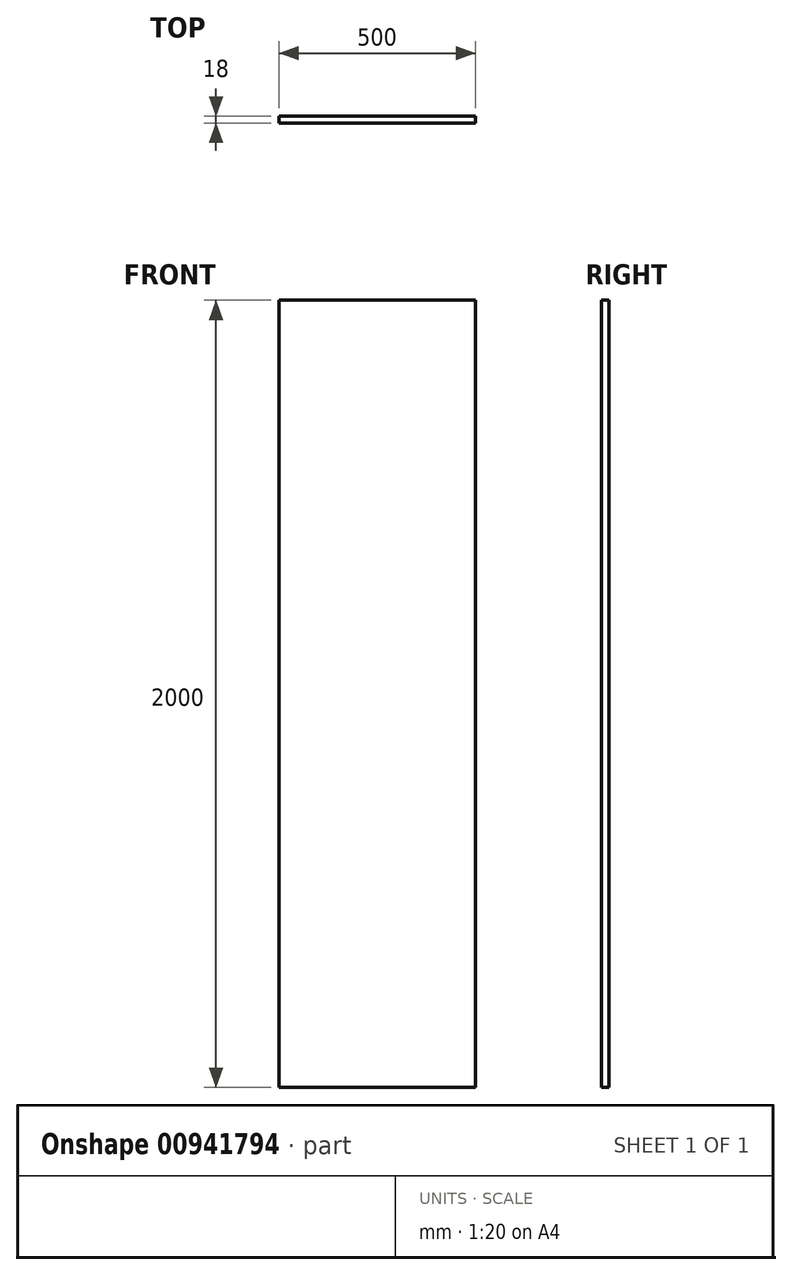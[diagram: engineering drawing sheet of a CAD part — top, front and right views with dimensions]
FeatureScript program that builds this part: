
annotation { "Feature Type Name" : "Feature", "Feature Type Description" : "" }
export const myFeature = defineFeature(function(context is Context, id is Id, definition is map)
    precondition{}
    {
        {
            var Q0;
            Q0=qCreatedBy(makeId("Front.planeOp"),FACE);
            var sketch = newSketch(context, id + "F0", { "sketchPlane" : qUnion([Q0])});
            skLineSegment(sketch, "E0.bottom", {"start": v(266.3, 1000) * mm, "end": v(-233.7, 1000) * mm});
            skLineSegment(sketch, "E0.top", {"start": v(266.3, -1000) * mm, "end": v(-233.7, -1000) * mm});
            skLineSegment(sketch, "E0.left", {"start": v(266.3, 1000) * mm, "end": v(266.3, -1000) * mm});
            skLineSegment(sketch, "E0.right", {"start": v(-233.7, 1000) * mm, "end": v(-233.7, -1000) * mm});
            skPoint(sketch, "E0.middle", {"position": v(16.3, 0) * mm});
            skSolve(sketch);
        }
        {
            var Q0;
            Q0=qSketchRegion(id+"F0",true);
            extrude(context, id + "F1", {"entities" : qUnion([Q0]), "endBound" : BoundingType.SYMMETRIC, "depth" : 18 * mm, "offsetDistance" : 25 * mm});
        }
    });
